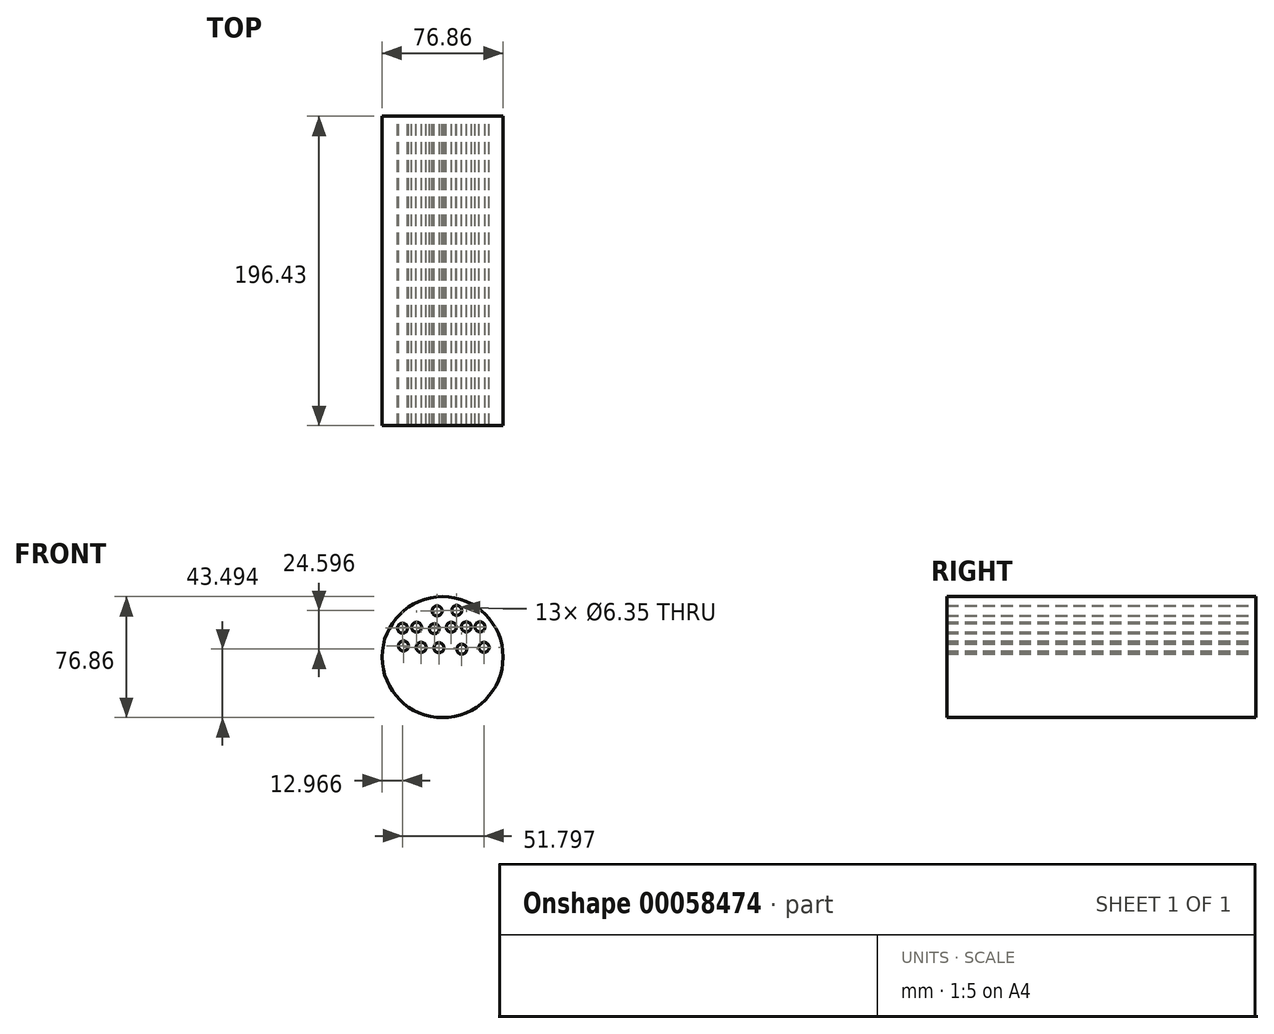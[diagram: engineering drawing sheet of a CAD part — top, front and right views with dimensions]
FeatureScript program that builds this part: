
annotation { "Feature Type Name" : "Feature", "Feature Type Description" : "" }
export const myFeature = defineFeature(function(context is Context, id is Id, definition is map)
    precondition{}
    {
        {
            var Q0;
            Q0=qCreatedBy(makeId("Front.planeOp"),FACE);
            var sketch = newSketch(context, id + "F0", { "sketchPlane" : qUnion([Q0])});
            skCircle(sketch, "E0", {"center": v(0, 0) * mm, "radius": 38.43 * mm});
            skSolve(sketch);
        }
        {
            var Q0;
            Q0=makeQuery(id+"F0.imprint","IMPRINT",FACE,{"disambiguationData":[TD([[makeQuery(id+"F0.imprint","IMPRINT",EDGE,{"derivedFrom":sQuery(id+"F0.wireOp",EDGE,"E0")}),1.0]])]});
            extrude(context, id + "F1", {"entities" : qUnion([Q0]), "depth" : 196.43 * mm});
        }
        {
            var Q0;
            Q0=makeQuery(id+"F1.opExtrude","CAP_FACE",FACE,{"disambiguationData":[OSD([sQuery(id+"F0.wireOp",EDGE,"E0")])],"isStart":true});
            var sketch = newSketch(context, id + "F2", { "sketchPlane" : qUnion([Q0])});
            skCircle(sketch, "E1", {"center": v(-8.97, 29.66) * mm, "radius": 4.14 * mm});
            skCircle(sketch, "E2", {"center": v(3.47, 29.37) * mm, "radius": 3.63 * mm});
            skCircle(sketch, "E3", {"center": v(-23.73, 19.24) * mm, "radius": 3.77 * mm});
            skCircle(sketch, "E4", {"center": v(-15.05, 19.24) * mm, "radius": 3.2 * mm});
            skCircle(sketch, "E5", {"center": v(-5.5, 18.95) * mm, "radius": 3.58 * mm});
            skCircle(sketch, "E6", {"center": v(5.2, 18.09) * mm, "radius": 4.27 * mm});
            skCircle(sketch, "E7", {"center": v(16.5, 18.95) * mm, "radius": 4.85 * mm});
            skCircle(sketch, "E8", {"center": v(25.46, 18.37) * mm, "radius": 3.12 * mm});
            skCircle(sketch, "E9", {"center": v(24.89, 7.09) * mm, "radius": 3.77 * mm});
            skCircle(sketch, "E10", {"center": v(13.6, 6.22) * mm, "radius": 4.43 * mm});
            skCircle(sketch, "E11", {"center": v(2.31, 5.93) * mm, "radius": 5.15 * mm});
            skCircle(sketch, "E12", {"center": v(-12.15, 5.06) * mm, "radius": 5.34 * mm});
            skCircle(sketch, "E13", {"center": v(-26.33, 6.22) * mm, "radius": 6.9 * mm});
            skSolve(sketch);
        }
        {
            var Q0;
            Q0=sQuery(id+"F2.wireOp",VERTEX,"E11.center");
            var Q1;
            Q1=sQuery(id+"F2.wireOp",VERTEX,"E12.center");
            var Q2;
            Q2=sQuery(id+"F2.wireOp",VERTEX,"E13.center");
            var Q3;
            Q3=sQuery(id+"F2.wireOp",VERTEX,"E10.center");
            var Q4;
            Q4=sQuery(id+"F2.wireOp",VERTEX,"E9.center");
            var Q5;
            Q5=sQuery(id+"F2.wireOp",VERTEX,"E8.center");
            var Q6;
            Q6=sQuery(id+"F2.wireOp",VERTEX,"E7.center");
            var Q7;
            Q7=sQuery(id+"F2.wireOp",VERTEX,"E6.center");
            var Q8;
            Q8=sQuery(id+"F2.wireOp",VERTEX,"E5.center");
            var Q9;
            Q9=sQuery(id+"F2.wireOp",VERTEX,"E4.center");
            var Q10;
            Q10=sQuery(id+"F2.wireOp",VERTEX,"E3.center");
            var Q11;
            Q11=sQuery(id+"F2.wireOp",VERTEX,"E1.center");
            var Q12;
            Q12=sQuery(id+"F2.wireOp",VERTEX,"E2.center");
            var Q13;
            Q13=makeQuery(id+"F1.opExtrude","SWEPT_BODY",BODY,{"disambiguationData":[OSD([sQuery(id+"F0.wireOp",EDGE,"E0")])]});
            hole(context, id + "F3", {"style" : HoleStyle.SIMPLE, "holeDiameter" : 6.35 * mm, "endStyle" : HoleEndStyle.THROUGH, "locations" : qUnion([Q0, Q1, Q2, Q3, Q4, Q5, Q6, Q7, Q8, Q9, Q10, Q11, Q12]), "scope" : qUnion([Q13])});
        }
    });
